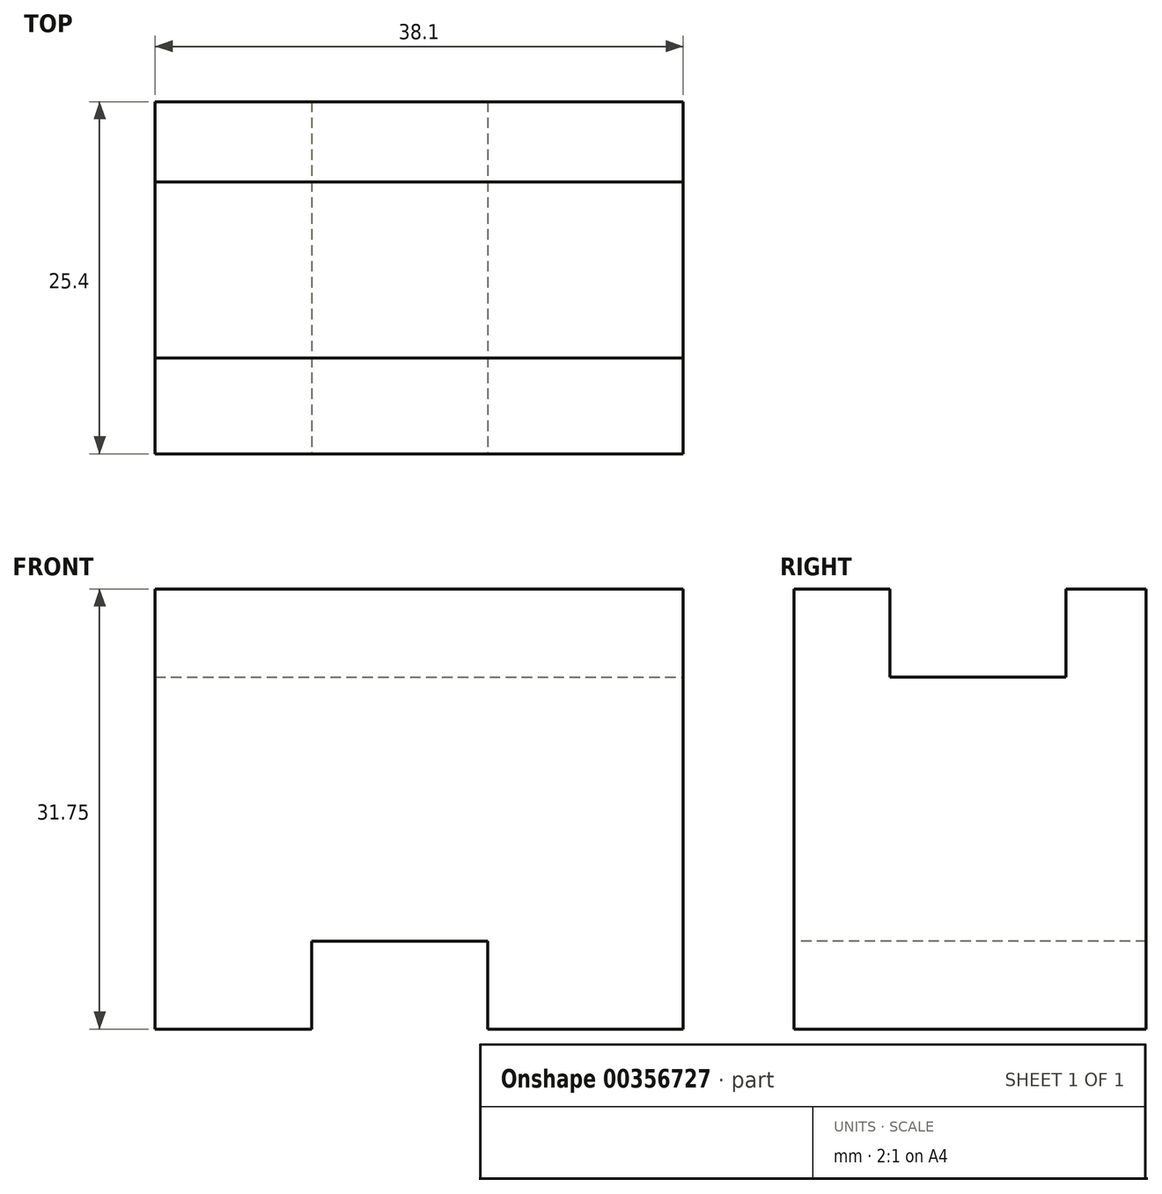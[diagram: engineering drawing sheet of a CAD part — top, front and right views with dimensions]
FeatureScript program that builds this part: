
annotation { "Feature Type Name" : "Feature", "Feature Type Description" : "" }
export const myFeature = defineFeature(function(context is Context, id is Id, definition is map)
    precondition{}
    {
        {
            var Q0;
            Q0=qCreatedBy(makeId("Right.planeOp"),FACE);
            var sketch = newSketch(context, id + "F0", { "sketchPlane" : qUnion([Q0])});
            skLineSegment(sketch, "E0", {"start": v(0, 0) * mm, "end": v(0, 31.75) * mm});
            skLineSegment(sketch, "E1", {"start": v(25.4, 31.75) * mm, "end": v(25.4, 0) * mm});
            skLineSegment(sketch, "E2", {"start": v(25.4, 0) * mm, "end": v(0, 0) * mm});
            skLineSegment(sketch, "E3", {"start": v(0, 31.75) * mm, "end": v(25.4, 31.75) * mm});
            skSolve(sketch);
        }
        {
            var Q0;
            Q0=makeQuery(id+"F0.imprint","IMPRINT",FACE,{"disambiguationData":[TD([[makeQuery(id+"F0.imprint","IMPRINT",EDGE,{"derivedFrom":sQuery(id+"F0.wireOp",EDGE,"E0")}),-1.0]])]});
            extrude(context, id + "F1", {"entities" : qUnion([Q0]), "depth" : 38.1 * mm});
        }
        {
            var Q0;
            Q0=makeQuery(id+"F1.opExtrude","CAP_FACE",FACE,{"disambiguationData":[OSD([sQuery(id+"F0.wireOp",EDGE,"E0"),sQuery(id+"F0.wireOp",EDGE,"E1"),sQuery(id+"F0.wireOp",EDGE,"E2"),sQuery(id+"F0.wireOp",EDGE,"E3")])],"isStart":false});
            var sketch = newSketch(context, id + "F2", { "sketchPlane" : qUnion([Q0])});
            skLineSegment(sketch, "E4", {"start": v(6.9, 31.75) * mm, "end": v(6.9, 25.4) * mm});
            skLineSegment(sketch, "E5", {"start": v(6.9, 25.4) * mm, "end": v(19.6, 25.4) * mm});
            skLineSegment(sketch, "E6", {"start": v(19.6, 25.4) * mm, "end": v(19.6, 31.75) * mm});
            skSolve(sketch);
        }
        {
            var Q0;
            {var subQ0=sQuery(id+"F2.wireOp",EDGE,"E4");Q0=makeQuery(id+"F2.imprint","IMPRINT",FACE,{"disambiguationData":[TD([[makeQuery(id+"F2.imprint","IMPRINT",EDGE,{"derivedFrom":subQ0}),1.0]])]});}
            extrude(context, id + "F3", {"entities" : qUnion([Q0]), "operationType" : NewBodyOperationType.REMOVE, "oppositeDirection" : true, "depth" : 38.1 * mm});
        }
        {
            var Q0;
            Q0=makeQuery(id+"F1.opExtrude","SWEPT_FACE",FACE,{"disambiguationData":[OSD([sQuery(id+"F0.wireOp",EDGE,"E0")])]});
            var sketch = newSketch(context, id + "F4", { "sketchPlane" : qUnion([Q0])});
            skLineSegment(sketch, "E7", {"start": v(11.3, 0) * mm, "end": v(11.3, 6.35) * mm});
            skLineSegment(sketch, "E8", {"start": v(11.3, 6.35) * mm, "end": v(24, 6.35) * mm});
            skLineSegment(sketch, "E9", {"start": v(24, 6.35) * mm, "end": v(24, 0) * mm});
            skSolve(sketch);
        }
        {
            var Q0;
            {var subQ0=sQuery(id+"F4.wireOp",EDGE,"E7");Q0=makeQuery(id+"F4.imprint","IMPRINT",FACE,{"disambiguationData":[TD([[makeQuery(id+"F4.imprint","IMPRINT",EDGE,{"derivedFrom":subQ0}),-1.0]])]});}
            extrude(context, id + "F5", {"entities" : qUnion([Q0]), "operationType" : NewBodyOperationType.REMOVE, "oppositeDirection" : true, "depth" : 25.4 * mm});
        }
    });
